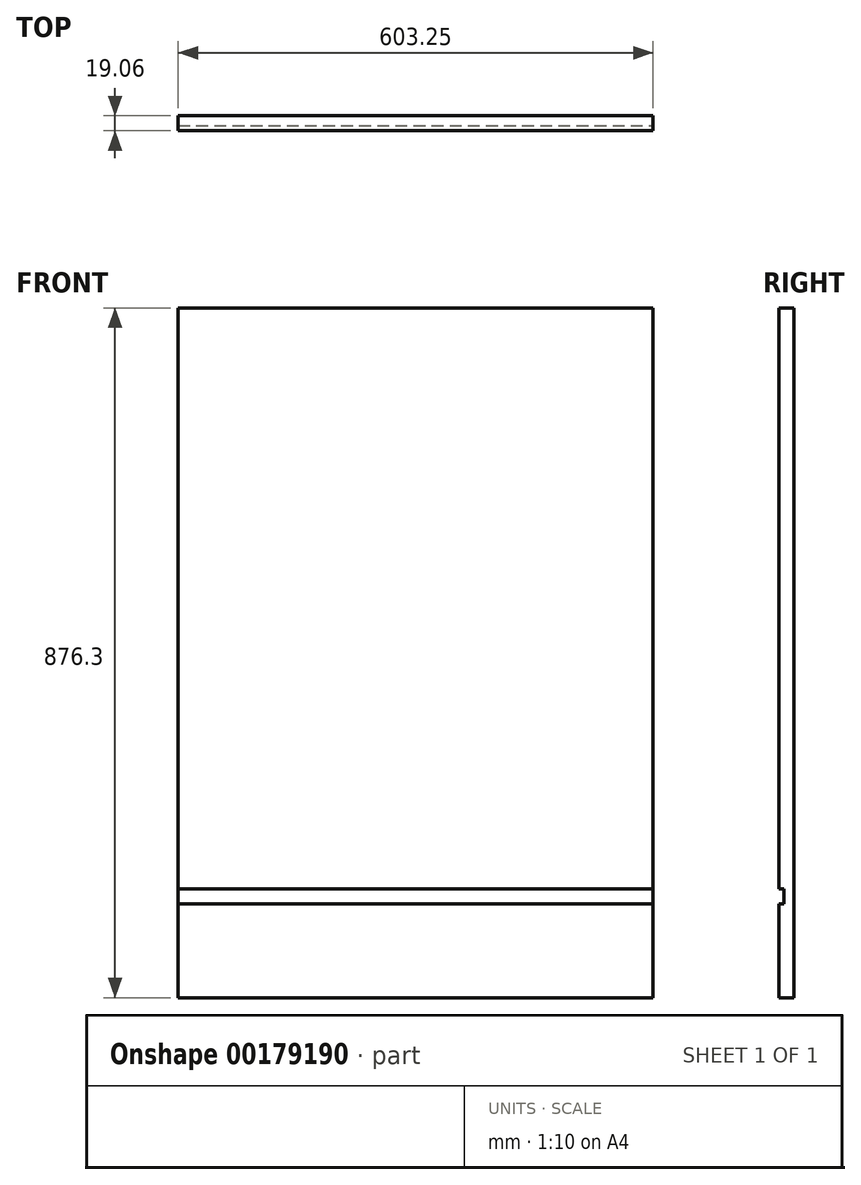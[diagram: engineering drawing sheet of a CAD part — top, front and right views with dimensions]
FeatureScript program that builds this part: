
annotation { "Feature Type Name" : "Feature", "Feature Type Description" : "" }
export const myFeature = defineFeature(function(context is Context, id is Id, definition is map)
    precondition{}
    {
        {
            var Q0;
            Q0=qCreatedBy(makeId("Front.planeOp"),FACE);
            var sketch = newSketch(context, id + "F0", { "sketchPlane" : qUnion([Q0])});
            skLineSegment(sketch, "E0.bottom", {"start": v(-247.9, 438.15) * mm, "end": v(355.35, 438.15) * mm});
            skLineSegment(sketch, "E0.top", {"start": v(-247.9, -438.15) * mm, "end": v(355.35, -438.15) * mm});
            skLineSegment(sketch, "E0.left", {"start": v(-247.9, 438.15) * mm, "end": v(-247.9, -438.15) * mm});
            skLineSegment(sketch, "E0.right", {"start": v(355.35, 438.15) * mm, "end": v(355.35, -438.15) * mm});
            skLineSegment(sketch, "E1", {"start": v(-247.9, 0) * mm, "end": v(355.35, 0) * mm});
            skSolve(sketch);
        }
        {
            var Q0;
            {var subQ0=sQuery(id+"F0.wireOp",EDGE,"E0.bottom");Q0=makeQuery(id+"F0.imprint","IMPRINT",FACE,{"disambiguationData":[TD([[makeQuery(id+"F0.imprint","IMPRINT",EDGE,{"derivedFrom":subQ0}),-1.0]])]});}
            var Q1;
            {var subQ0=sQuery(id+"F0.wireOp",EDGE,"E0.top");Q1=makeQuery(id+"F0.imprint","IMPRINT",FACE,{"disambiguationData":[TD([[makeQuery(id+"F0.imprint","IMPRINT",EDGE,{"derivedFrom":subQ0}),1.0]])]});}
            extrude(context, id + "F1", {"entities" : qUnion([Q0, Q1]), "depth" : 19.05 * mm, "symmetric" : true});
        }
        {
            var Q0;
            Q0=makeQuery(id+"F1.opExtrude","CAP_FACE",FACE,{"disambiguationData":[OSD([sQuery(id+"F0.wireOp",EDGE,"E0.bottom"),sQuery(id+"F0.wireOp",EDGE,"E0.top"),sQuery(id+"F0.wireOp",EDGE,"E0.left"),sQuery(id+"F0.wireOp",EDGE,"E0.right")])],"isStart":false});
            var sketch = newSketch(context, id + "F2", { "sketchPlane" : qUnion([Q0])});
            skLineSegment(sketch, "E2.bottom", {"start": v(355.35, 438.15) * mm, "end": v(336.3, 438.15) * mm});
            skLineSegment(sketch, "E2.top", {"start": v(355.35, -438.15) * mm, "end": v(336.3, -438.15) * mm});
            skLineSegment(sketch, "E2.left", {"start": v(355.35, 438.15) * mm, "end": v(355.35, -438.15) * mm});
            skLineSegment(sketch, "E2.right", {"start": v(336.3, 438.15) * mm, "end": v(336.3, -438.15) * mm});
            skSolve(sketch);
        }
        {
            var Q0;
            {var subQ0=sQuery(id+"F2.wireOp",EDGE,"E2.right");Q0=makeQuery(id+"F2.imprint","IMPRINT",FACE,{"disambiguationData":[TD([[makeQuery(id+"F2.imprint","IMPRINT",EDGE,{"derivedFrom":subQ0}),-1.0]])]});}
            var sketch = newSketch(context, id + "F3", { "sketchPlane" : qUnion([Q0])});
            skLineSegment(sketch, "E3.bottom", {"start": v(-247.9, -300.04) * mm, "end": v(355.35, -300.04) * mm});
            skLineSegment(sketch, "E3.top", {"start": v(-247.9, -319.09) * mm, "end": v(355.35, -319.09) * mm});
            skLineSegment(sketch, "E3.left", {"start": v(-247.9, -300.04) * mm, "end": v(-247.9, -319.09) * mm});
            skLineSegment(sketch, "E3.right", {"start": v(355.35, -300.04) * mm, "end": v(355.35, -319.09) * mm});
            skSolve(sketch);
        }
        {
            var Q0;
            Q0=qSketchRegion(id+"F3",true);
            extrude(context, id + "F4", {"entities" : qUnion([Q0]), "operationType" : NewBodyOperationType.REMOVE, "oppositeDirection" : true, "depth" : 6.35 * mm});
        }
    });
